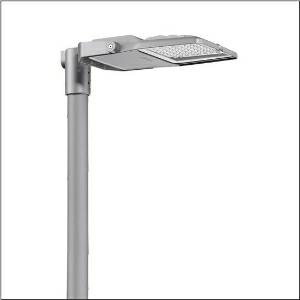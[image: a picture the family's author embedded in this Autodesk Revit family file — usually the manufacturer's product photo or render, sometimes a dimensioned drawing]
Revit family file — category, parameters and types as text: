
# Revit family: floodlight_fl_21_iq_mini___pl64_5xa7772c4e3a_b66a
name_source: partatom
category: Lighting Fixtures
units: mm (PartAtom-declared; Revit-internal decimal feet)

## family parameters
Cut with Voids When Loaded = No
Host = Face
Light Source = No
Part Type = Normal
Room Calculation Point = No
Round Connector Dimension = Use Diameter
Shared = No

## types (1)
- --- (1 x LED, 12280 lm, 87.2 W, 4000K)
    Apparent Load = 87 VA
    CIE Flux Codes = 28 80 98 100 100
    Color Rendering = 70
    Color Temperature = 4000K
    Default Elevation = 1800 mm
    Description = Floodlight FL 21 iQ mini, floodlight, primary light control with lens, of PMMA, primary optical cover: protective disc, of toughened safety glass, transparent, light distribution: PL64, light emission: direct distribution, installation type: surface-mounted, LED, High Power LED, rated luminous flux: 12.280lm, luminous efficacy: 141lm/W, light colour: 740, colour temperature: 4000K, control gear: iQ Street-Remote/DALI, control: Auto-Match, Temp-Guard, Night-Set, Smart-Wire, Desk-Remote (wireless, voltage-free reading and setting of iQ features in the workshop via application-optimized NFC function/RFID function), optimised constant luminous flux control (CLO 2.0), Light-Fading, Lumen-Switch, with terminal, 6-pole, mains connection: 220..240V, AC, 50/60Hz, start of lifetime: 87W, end of service life: 92W, reduction: 40W, luminaire housing, of diecast aluminium, powder-coated, Siteco® metallic grey (DB 702S), corrosivity category C5 mid according to DIN EN ISO 12944, suitable for swimming pools, chlorine-resistant, sealing non-destructively replaceable, please order mast flange separately, mast bracket, of steel, galvanised, powder-coated, protection rating (complete): IP66, insulation class (complete): insulation class II (safety insulation), certification: CE, ENEC, VDE, protection symbol: D, impact resistance: IK08, permissible operating ambient temperature: -40..+40°C, permissible operating ambient temperature for outdoor applications: -40..+50°C, standard: DIN EN 12944, LABS conformity tested according to VDMA 24364:2018-05, packaging unit: 1 piece

Light Distribution: PL64
    Height = 70 mm
    Lamp = 1 x LED
    Lamp Light Flux = 12280 lm
    Lamp Power = 87.2 W
    Lamp count = 1
    Length = 485 mm
    Luminous efficacy = 141 lm/W
    Manufacturer = Siteco
    ModVariant = No
    Model = 5XA7772C4E3A
    Number of Poles = 1
    OnlyDefault = Yes
    Power Factor = 1
    Product Name = Floodlight FL 21 iQ mini | PL64
    Product group = floodlight | pylon annexe
    ProductGroupID = 6200
    Protection Class = Protection class II
    Protection Degree = IP 66
    RLX_Detail_Level = 1
    RLX_Emergency_Light_Flux = 0 lm
    RLX_Emergency_Type = 0
    RLX_Emergency_Type_DB = No
    RlxData = <blob elided: 101433 chars, md5=6e17e0fe>
    Socket = socket
    Standby Power = 0 W
    System Light Flux = 12280 lm
    System Power = 87 W
    Type Comments = factory setting: luminous flux: 100 % | dim-lin: 254 | 456 mA
    Type Image = l_1007125.jpg
    URL = http://relux.com
    VarID = @adj_166218
    Voltage = 0 V
    Weight = 0.00 kg
    Width = 337 mm

## geometry (parser evidence)
native form markers: Blend x4, Sweep x13
no freeform markers — native parametric forms only
